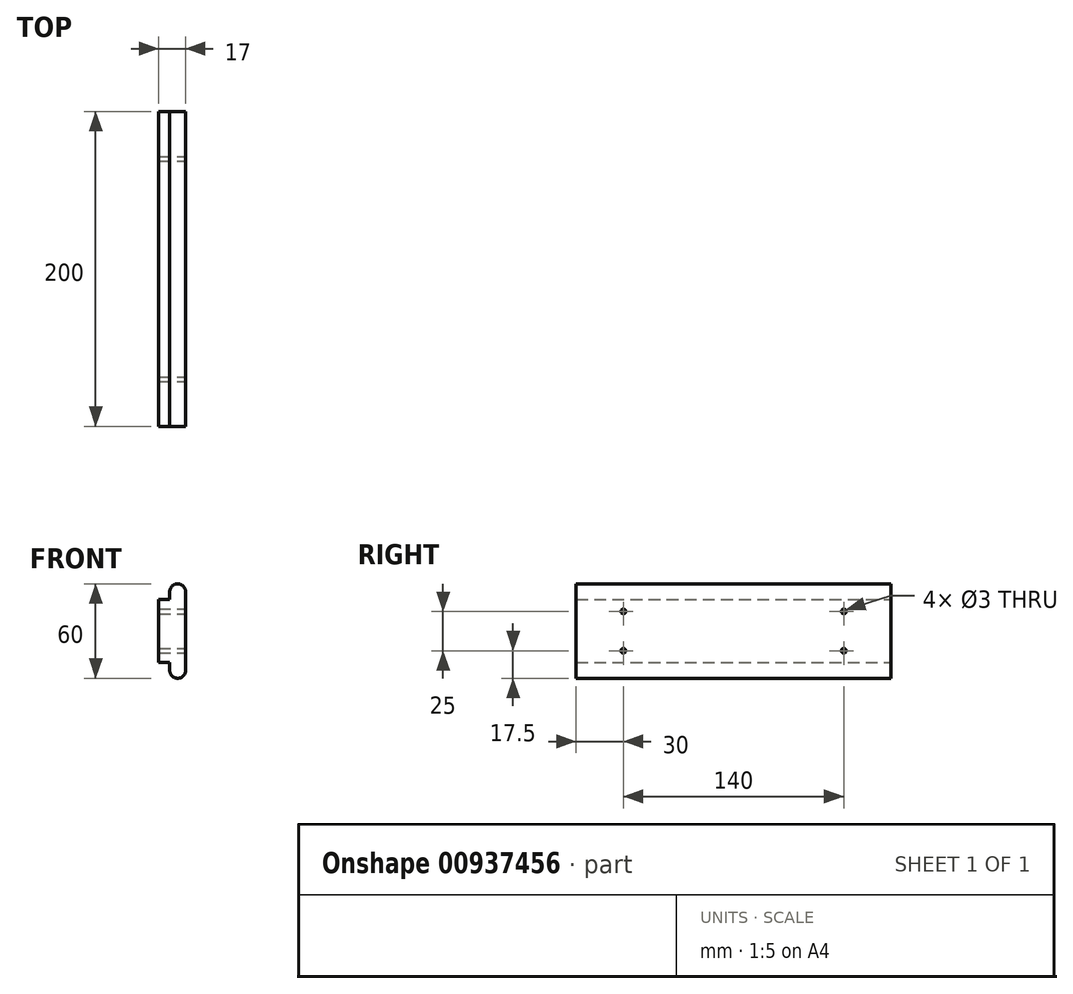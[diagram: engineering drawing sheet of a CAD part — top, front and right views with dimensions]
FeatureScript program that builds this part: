
annotation { "Feature Type Name" : "Feature", "Feature Type Description" : "" }
export const myFeature = defineFeature(function(context is Context, id is Id, definition is map)
    precondition{}
    {
        {
            var Q0;
            Q0=qCreatedBy(makeId("Front.planeOp"),FACE);
            var sketch = newSketch(context, id + "F0", { "sketchPlane" : qUnion([Q0])});
            skLineSegment(sketch, "E0.bottom", {"start": v(0, 0) * mm, "end": v(10, 0) * mm});
            skLineSegment(sketch, "E0.top", {"start": v(0, 50) * mm, "end": v(10, 50) * mm});
            skLineSegment(sketch, "E0.left", {"start": v(0, 0) * mm, "end": v(0, 50) * mm});
            skLineSegment(sketch, "E0.right", {"start": v(10, 0) * mm, "end": v(10, 50) * mm});
            skLineSegment(sketch, "E1", {"start": v(0, 50) * mm, "end": v(0, 45) * mm});
            skLineSegment(sketch, "E2", {"start": v(0, 0) * mm, "end": v(0, 5) * mm});
            skLineSegment(sketch, "E3.bottom", {"start": v(0, 45) * mm, "end": v(-7, 45) * mm});
            skLineSegment(sketch, "E3.top", {"start": v(0, 5) * mm, "end": v(-7, 5) * mm});
            skLineSegment(sketch, "E3.left", {"start": v(0, 45) * mm, "end": v(0, 5) * mm});
            skLineSegment(sketch, "E3.right", {"start": v(-7, 45) * mm, "end": v(-7, 5) * mm});
            skCircle(sketch, "E4", {"center": v(5, 50) * mm, "radius": 5 * mm});
            skCircle(sketch, "E5", {"center": v(5, 0) * mm, "radius": 5 * mm});
            skSolve(sketch);
        }
        {
            var Q0;
            Q0=makeQuery(id+"F0.imprint","IMPRINT",FACE,{"disambiguationData":[TD([[makeQuery(id+"F0.imprint","IMPRINT",EDGE,{"derivedFrom":sQuery(id+"F0.wireOp",EDGE,"E3.bottom")}),1.0]])]});
            var Q1;
            {var subQ0=sQuery(id+"F0.wireOp",EDGE,"E0.bottom");Q1=makeQuery(id+"F0.imprint","IMPRINT",FACE,{"disambiguationData":[TD([[makeQuery(id+"F0.imprint","IMPRINT",EDGE,{"derivedFrom":subQ0}),-1.0]])]});}
            var Q2;
            {var subQ0=sQuery(id+"F0.wireOp",EDGE,"E0.bottom");Q2=makeQuery(id+"F0.imprint","IMPRINT",FACE,{"disambiguationData":[TD([[makeQuery(id+"F0.imprint","IMPRINT",EDGE,{"derivedFrom":subQ0}),1.0]])]});}
            var Q3;
            {var subQ0=sQuery(id+"F0.wireOp",EDGE,"E0.top");Q3=makeQuery(id+"F0.imprint","IMPRINT",FACE,{"disambiguationData":[TD([[makeQuery(id+"F0.imprint","IMPRINT",EDGE,{"derivedFrom":subQ0}),-1.0]])]});}
            var Q4;
            {var subQ0=sQuery(id+"F0.wireOp",EDGE,"E0.top");Q4=makeQuery(id+"F0.imprint","IMPRINT",FACE,{"disambiguationData":[TD([[makeQuery(id+"F0.imprint","IMPRINT",EDGE,{"derivedFrom":subQ0}),1.0]])]});}
            var Q5;
            {var subQ2=sQuery(id+"F0.wireOp",EDGE,"E0.right");Q5=makeQuery(id+"F0.imprint","IMPRINT",FACE,{"disambiguationData":[TD([[makeQuery(id+"F0.imprint","IMPRINT",EDGE,{"derivedFrom":subQ2}),1.0]])]});}
            extrude(context, id + "F1", {"entities" : qUnion([Q0, Q1, Q2, Q3, Q4, Q5]), "depth" : 200 * mm, "offsetDistance" : 25 * mm});
        }
        {
            var Q0;
            Q0=makeQuery(id+"F1.opExtrude","SWEPT_FACE",FACE,{"disambiguationData":[OSD([sQuery(id+"F0.wireOp",EDGE,"E0.right")])]});
            var sketch = newSketch(context, id + "F2", { "sketchPlane" : qUnion([Q0])});
            skLineSegment(sketch, "E6", {"start": v(-200, 50) * mm, "end": v(-170, 50) * mm});
            skLineSegment(sketch, "E7", {"start": v(-170, 50) * mm, "end": v(-170, 37.5) * mm});
            skLineSegment(sketch, "E8", {"start": v(-200, 0) * mm, "end": v(-170, 0) * mm});
            skLineSegment(sketch, "E9", {"start": v(-170, 0) * mm, "end": v(-170, 12.5) * mm});
            skLineSegment(sketch, "E10", {"start": v(0, 50) * mm, "end": v(-30, 50) * mm});
            skLineSegment(sketch, "E11", {"start": v(-30, 50) * mm, "end": v(-30, 37.5) * mm});
            skLineSegment(sketch, "E12", {"start": v(0, 0) * mm, "end": v(-30, 0) * mm});
            skLineSegment(sketch, "E13", {"start": v(-30, 0) * mm, "end": v(-30, 12.5) * mm});
            skCircle(sketch, "E14", {"center": v(-170, 37.5) * mm, "radius": 1.5 * mm});
            skCircle(sketch, "E15", {"center": v(-170, 12.5) * mm, "radius": 1.5 * mm});
            skCircle(sketch, "E16", {"center": v(-30, 12.5) * mm, "radius": 1.5 * mm});
            skCircle(sketch, "E17", {"center": v(-30, 37.5) * mm, "radius": 1.5 * mm});
            skSolve(sketch);
        }
        {
            var Q0;
            Q0=makeQuery(id+"F2.imprint","IMPRINT",FACE,{"disambiguationData":[TD([[makeQuery(id+"F2.imprint","IMPRINT",EDGE,{"derivedFrom":sQuery(id+"F2.wireOp",EDGE,"E14")}),1.0]])]});
            var Q1;
            Q1=makeQuery(id+"F2.imprint","IMPRINT",FACE,{"disambiguationData":[TD([[makeQuery(id+"F2.imprint","IMPRINT",EDGE,{"derivedFrom":sQuery(id+"F2.wireOp",EDGE,"E15")}),1.0]])]});
            var Q2;
            Q2=makeQuery(id+"F2.imprint","IMPRINT",FACE,{"disambiguationData":[TD([[makeQuery(id+"F2.imprint","IMPRINT",EDGE,{"derivedFrom":sQuery(id+"F2.wireOp",EDGE,"E16")}),1.0]])]});
            var Q3;
            Q3=makeQuery(id+"F2.imprint","IMPRINT",FACE,{"disambiguationData":[TD([[makeQuery(id+"F2.imprint","IMPRINT",EDGE,{"derivedFrom":sQuery(id+"F2.wireOp",EDGE,"E17")}),1.0]])]});
            extrude(context, id + "F3", {"entities" : qUnion([Q0, Q1, Q2, Q3]), "operationType" : NewBodyOperationType.REMOVE, "oppositeDirection" : true, "depth" : 25 * mm, "offsetDistance" : 25 * mm});
        }
    });
